FCSTD DOCUMENT  (FreeCAD 0.19R24291 (Git))
Label: Problem02
License: All rights reserved
LicenseURL: http://en.wikipedia.org/wiki/All_rights_reserved
objects: App::FeaturePython×44, Part::Part2DObjectPython×14, Part::Mirroring×13, Part::FeaturePython×1
note: 27 computed .brp shape members not serialized (recipe doc carries the construction recipe); baked Part::Feature solids carry a one-line shape summary decoded from their .brp

FEATURE [Part::Part2DObjectPython] Circle  # Draft 2D object (typed FeaturePython)
  Area = 0
  FirstAngle = 0
  LastAngle = 0
  MakeFace = false
  Radius = 40
FEATURE [Part::Part2DObjectPython] Circle001  # Draft 2D object (typed FeaturePython)
  Area = 0
  FirstAngle = 0
  LastAngle = 0
  MakeFace = false
  Radius = 60
FEATURE [Part::Part2DObjectPython] Line  # Draft 2D object (typed FeaturePython)
  Area = 0
  ChamferSize = 0
  Closed = false
  End = (7.3e-15,-60,0)
  FilletRadius = 0
  Length = 120
  MakeFace = false
  Placement = pos=(0,60,0) rot=(0,0,1;0rad)
  Points = (2) [(0,0,0),(3.67394e-15,-120,0)]
  Start = (0,60,0)
  Subdivisions = 0
FEATURE [Part::Part2DObjectPython] Line001  # Draft 2D object (typed FeaturePython)
  Area = 0
  ChamferSize = 0
  Closed = false
  End = (60,3.7e-15,0)
  FilletRadius = 0
  Length = 120
  MakeFace = false
  Placement = pos=(-60,-1.1e-14,0) rot=(0,0,1;0rad)
  Points = (2) [(0,0,0),(120,1.10218e-14,0)]
  Start = (-60,-1.1e-14,0)
  Subdivisions = 0
FEATURE [Part::FeaturePython] Array  # Draft array (typed FeaturePython)
  Angle = 360
  ArrayType = 1
  Axis = (0,0,1)
  Center = (0,0,0)
  Count = 12
  ExpandArray = false
  Fuse = false
  IntervalAxis = (0,0,0)
  IntervalX = (50,0,0)
  IntervalY = (0,50,0)
  IntervalZ = (0,0,50)
  NumberCircles = 3
  NumberPolar = 12
  NumberX = 2
  NumberY = 2
  NumberZ = 1
  PlacementList = 12 placements: [(-60,-1.10218e-14,0),(-51.9615,-30,0),(-30,-51.9615,0),(1.42109e-14,-60,0),(30,-51.9615,0),(51.9615,-30,0),(60,3.67394e-15,0),(51.9615,30,0),(30,51.9615,0),(0,60,0),(-30,51.9615,0),(-51.9615,30,0)]
  RadialDistance = 50
  ScaleList = (12) [(1,1,1),(1,1,1),(1,1,1),(1,1,1),(1,1,1),(1,1,1),(1,1,1),(1,1,1),(1,1,1),(1,1,1),(1,1,1),(1,1,1)]
  Symmetry = 1
  TangentialDistance = 25
FEATURE [Part::Part2DObjectPython] Line004  # Draft 2D object (typed FeaturePython)
  Area = 0
  ChamferSize = 0
  Closed = false
  End = (-34.641,20,0)
  FilletRadius = 0
  Length = 18.3473
  MakeFace = false
  Placement = pos=(-34.641,20,0) rot=(0,0,1;0rad)
  Points = (2) [(-18.3473,3.55271e-15,0),(0,0,0)]
  Start = (-52.9883,20,0)
  Subdivisions = 0
FEATURE [Part::Part2DObjectPython] Line005  # Draft 2D object (typed FeaturePython)
  Area = 0
  ChamferSize = 0
  Closed = false
  End = (-20,34.641,0)
  FilletRadius = 0
  Length = 11.1816
  MakeFace = false
  Placement = pos=(-20,34.641,0) rot=(0,0,1;0rad)
  Points = (2) [(-11.1816,0,0),(0,0,0)]
  Start = (-31.1816,34.641,0)
  Subdivisions = 0
FEATURE [Part::Part2DObjectPython] Line006  # Draft 2D object (typed FeaturePython)
  Area = 0
  ChamferSize = 0
  Closed = false
  End = (-30,51.7655,0)
  FilletRadius = 0
  Length = 18.1383
  MakeFace = false
  Placement = pos=(-30,12.8473,0) rot=(0,0,1;3.14159rad)
  Points = (2) [(3.55271e-15,-20.7799,0),(3.55271e-15,-38.9182,0)]
  Start = (-30,33.6272,0)
  Subdivisions = 0
FEATURE [Part::Part2DObjectPython] Line007  # Draft 2D object (typed FeaturePython)
  Area = 0
  ChamferSize = 0
  Closed = false
  End = (-51.9615,30,0)
  FilletRadius = 0
  Length = 11.2503
  MakeFace = false
  Placement = pos=(-51.9615,30,0) rot=(0,0,1;0rad)
  Points = (2) [(-7.10543e-15,-11.2503,0),(0,-3.55271e-15,0)]
  Start = (-51.9615,18.7497,0)
  Subdivisions = 0
FEATURE [Part::Mirroring] mirror  label="Line004 (mirrored)"
  Base = (0,60,0)
  Normal = (-1,1e-16,0)
  Source = -> Line004
FEATURE [Part::Mirroring] mirror001  label="Line007 (mirrored)"
  Base = (0,60,0)
  Normal = (-1,1e-16,0)
  Source = -> Line007
FEATURE [Part::Mirroring] mirror002  label="Line005 (mirrored)"
  Base = (0,60,0)
  Normal = (-1,1e-16,0)
  Source = -> Line005
FEATURE [Part::Mirroring] mirror003  label="Line006 (mirrored)"
  Base = (0,60,0)
  Normal = (-1,1e-16,0)
  Source = -> Line006
FEATURE [Part::Mirroring] mirror004  label="Line002 (mirrored)"
  Base = (-60,3.7e-15,0)
  Normal = (0,-1,0)
FEATURE [Part::Mirroring] mirror005  label="Line004 (mirrored)001"
  Base = (-60,3.7e-15,0)
  Normal = (0,-1,0)
  Source = -> Line004
FEATURE [Part::Mirroring] mirror006  label="Line007 (mirrored)001"
  Base = (-60,3.7e-15,0)
  Normal = (0,-1,0)
  Source = -> Line007
FEATURE [Part::Mirroring] mirror007  label="Line005 (mirrored)001"
  Base = (-60,3.7e-15,0)
  Normal = (0,-1,0)
  Source = -> Line005
FEATURE [Part::Mirroring] mirror008  label="Line006 (mirrored)001"
  Base = (-60,3.7e-15,0)
  Normal = (0,-1,0)
  Source = -> Line006
FEATURE [Part::Mirroring] mirror009  label="Line004 (mirrored)001 (mirrored)"
  Base = (-1.1e-14,-60,0)
  Normal = (1,-1e-16,0)
  Source = -> mirror005
FEATURE [Part::Mirroring] mirror010  label="Line007 (mirrored)001 (mirrored)"
  Base = (-1.1e-14,-60,0)
  Normal = (1,-1e-16,0)
  Source = -> mirror006
FEATURE [Part::Mirroring] mirror011  label="Line005 (mirrored)001 (mirrored)"
  Base = (-1.1e-14,-60,0)
  Normal = (1,-1e-16,0)
  Source = -> mirror007
FEATURE [Part::Mirroring] mirror012  label="Line006 (mirrored)001 (mirrored)"
  Base = (-1.1e-14,-60,0)
  Normal = (1,-1e-16,0)
  Source = -> mirror008
FEATURE [Part::Part2DObjectPython] BSpline  # Draft 2D object (typed FeaturePython)
  Area = 0
  Closed = true
  MakeFace = false
  Parameterization = 1
  Points = (12) [(-60,1.83697e-14,0),(-51.9615,20,0),(-30,34.641,0),(-6.43249e-15,40,0),(30,34.641,0),(51.9615,20,0),(60,3.67394e-15,0),(51.9615,-20,0),(30,-34.641,0),+3 more]
FEATURE [App::FeaturePython] Dimension  # Draft dimension (typed FeaturePython)
  Diameter = false
  Dimline = (45.3041,74.677,0)
  Direction = (0,0,0)
  Distance = 120
  End = (60,3.7e-15,0)
  Normal = (0,0,1)
  Start = (-60,-1.1e-14,0)
FEATURE [App::FeaturePython] Dimension001  # Draft dimension (typed FeaturePython)
  Diameter = false
  Dimline = (80.4023,-18.6692,0)
  Direction = (0,0,0)
  Distance = 80
  End = (-7.3e-15,-40,0)
  Normal = (0,0,1)
  Start = (-6.4e-15,40,0)
FEATURE [App::FeaturePython] Text  # WARN: FeaturePython — macro-defined, semantics opaque (R4)
  Placement = pos=(-55.7588,31.1154,0) rot=(0,0,1;0rad)
  Text = 1
FEATURE [App::FeaturePython] Text001  # WARN: FeaturePython — macro-defined, semantics opaque (R4)
  Placement = pos=(-33.8536,54.5142,0) rot=(0,0,1;0rad)
  Text = 2
FEATURE [App::FeaturePython] Text002  # WARN: FeaturePython — macro-defined, semantics opaque (R4)
  Placement = pos=(-1.49352,63.7244,0) rot=(0,0,1;0rad)
  Text = 3
FEATURE [App::FeaturePython] Text003  # WARN: FeaturePython — macro-defined, semantics opaque (R4)
  Placement = pos=(32.1111,54.0164,0) rot=(0,0,1;0rad)
  Text = 4
FEATURE [App::FeaturePython] Text004  # WARN: FeaturePython — macro-defined, semantics opaque (R4)
  Placement = pos=(55.261,30.8665,0) rot=(0,0,1;0rad)
  Text = 5
FEATURE [App::FeaturePython] Text005  # WARN: FeaturePython — macro-defined, semantics opaque (R4)
  Placement = pos=(61.4023,1.71218,0) rot=(0,0,1;0rad)
  Text = 6
FEATURE [App::FeaturePython] Text006  # WARN: FeaturePython — macro-defined, semantics opaque (R4)
  Placement = pos=(54.0164,-34.1025,0) rot=(0,0,1;0rad)
  Text = 7
FEATURE [App::FeaturePython] Text007  # WARN: FeaturePython — macro-defined, semantics opaque (R4)
  Placement = pos=(29.1241,-57.0034,0) rot=(0,0,1;0rad)
  Text = 8
FEATURE [App::FeaturePython] Text008  # WARN: FeaturePython — macro-defined, semantics opaque (R4)
  Placement = pos=(-1.74242,-66.4625,0) rot=(0,0,1;0rad)
  Text = 9
FEATURE [App::FeaturePython] Text009  # WARN: FeaturePython — macro-defined, semantics opaque (R4)
  Placement = pos=(-33.3557,-57.7502,0) rot=(0,0,1;0rad)
  Text = 10
FEATURE [App::FeaturePython] Text010  # WARN: FeaturePython — macro-defined, semantics opaque (R4)
  Placement = pos=(-56.2566,-34.1025,0) rot=(0,0,1;0rad)
  Text = 11
FEATURE [App::FeaturePython] Text011  # WARN: FeaturePython — macro-defined, semantics opaque (R4)
  Placement = pos=(-67.2093,-5.47628,0) rot=(0,0,1;0rad)
  Text = 12
FEATURE [App::FeaturePython] Text012  # WARN: FeaturePython — macro-defined, semantics opaque (R4)
  Placement = pos=(-63.4754,1.24465,0) rot=(0,0,1;0rad)
  Text = A
FEATURE [App::FeaturePython] Text013  # WARN: FeaturePython — macro-defined, semantics opaque (R4)
  Placement = pos=(1.24462,2.73819,0) rot=(0,0,1;0rad)
  Text = O
FEATURE [App::FeaturePython] Text014  # WARN: FeaturePython — macro-defined, semantics opaque (R4)
  Placement = pos=(61.4023,-4.36853,0) rot=(0,0,1;0rad)
  Text = B
FEATURE [App::FeaturePython] Text015  # WARN: FeaturePython — macro-defined, semantics opaque (R4)
  Placement = pos=(-59.2509,-4.7914,0) rot=(0,0,1;0rad)
  Text = P12
FEATURE [App::FeaturePython] Text016  # WARN: FeaturePython — macro-defined, semantics opaque (R4)
  Placement = pos=(-51.6501,14.3628,0) rot=(0,0,1;0rad)
  Text = P1
FEATURE [App::FeaturePython] Text017  # WARN: FeaturePython — macro-defined, semantics opaque (R4)
  Placement = pos=(-33.4079,29.5646,0) rot=(0,0,1;0rad)
  Text = P2
FEATURE [App::FeaturePython] Text018  # WARN: FeaturePython — macro-defined, semantics opaque (R4)
  Placement = pos=(-6.6528,35.6453,0) rot=(0,0,1;0rad)
  Text = P3
FEATURE [App::FeaturePython] Text019  # WARN: FeaturePython — macro-defined, semantics opaque (R4)
  Placement = pos=(28.0073,28.6525,0) rot=(0,0,1;0rad)
  Text = P4
FEATURE [App::FeaturePython] Text020  # WARN: FeaturePython — macro-defined, semantics opaque (R4)
  Placement = pos=(48.0737,13.4507,0) rot=(0,0,1;0rad)
  Text = P5
FEATURE [App::FeaturePython] Text021  # WARN: FeaturePython — macro-defined, semantics opaque (R4)
  Placement = pos=(53.2423,-5.09545,0) rot=(0,0,1;0rad)
  Text = P6
FEATURE [App::FeaturePython] Text022  # WARN: FeaturePython — macro-defined, semantics opaque (R4)
  Placement = pos=(46.8575,-17.8649,0) rot=(0,0,1;0rad)
  Text = P7
FEATURE [App::FeaturePython] Text023  # WARN: FeaturePython — macro-defined, semantics opaque (R4)
  Placement = pos=(27.3992,-33.0667,0) rot=(0,0,1;0rad)
  Text = P8
FEATURE [App::FeaturePython] Text024  # WARN: FeaturePython — macro-defined, semantics opaque (R4)
  Placement = pos=(-6.04468,-37.6273,0) rot=(0,0,1;0rad)
  Text = P9
FEATURE [App::FeaturePython] Text025  # WARN: FeaturePython — macro-defined, semantics opaque (R4)
  Placement = pos=(-33.4079,-32.7627,0) rot=(0,0,1;0rad)
  Text = P10
FEATURE [App::FeaturePython] Text026  # WARN: FeaturePython — macro-defined, semantics opaque (R4)
  Placement = pos=(-51.65,-17.8649,0) rot=(0,0,1;0rad)
  Text = P11
FEATURE [App::FeaturePython] Text027  # WARN: FeaturePython — macro-defined, semantics opaque (R4)
  Placement = pos=(-31.8877,18.9234,0) rot=(0,0,1;0rad)
  Text = 1'
FEATURE [App::FeaturePython] Text028  # WARN: FeaturePython — macro-defined, semantics opaque (R4)
  Placement = pos=(-18.2061,31.0848,0) rot=(0,0,1;0rad)
  Text = 2'
FEATURE [App::FeaturePython] Text029  # WARN: FeaturePython — macro-defined, semantics opaque (R4)
  Placement = pos=(1.55618,34.1252,0) rot=(0,0,1;0rad)
  Text = 3'
FEATURE [App::FeaturePython] Text030  # WARN: FeaturePython — macro-defined, semantics opaque (R4)
  Placement = pos=(19.4943,26.8283,0) rot=(0,0,1;0rad)
  Text = 4'
FEATURE [App::FeaturePython] Text031  # WARN: FeaturePython — macro-defined, semantics opaque (R4)
  Placement = pos=(31.3517,14.6669,0) rot=(0,0,1;0rad)
  Text = 5'
FEATURE [App::FeaturePython] Text032  # WARN: FeaturePython — macro-defined, semantics opaque (R4)
  Placement = pos=(35.6082,0.985281,0) rot=(0,0,1;0rad)
  Text = 6'
FEATURE [App::FeaturePython] Text033  # WARN: FeaturePython — macro-defined, semantics opaque (R4)
  Placement = pos=(32.5678,-17.5609,0) rot=(0,0,1;0rad)
  Text = 7'
FEATURE [App::FeaturePython] Text034  # WARN: FeaturePython — macro-defined, semantics opaque (R4)
  Placement = pos=(19.7983,-31.2425,0) rot=(0,0,1;0rad)
  Text = 8'
FEATURE [App::FeaturePython] Text035  # WARN: FeaturePython — macro-defined, semantics opaque (R4)
  Placement = pos=(0.948107,-38.8434,0) rot=(0,0,1;0rad)
  Text = 9'
FEATURE [App::FeaturePython] Text036  # WARN: FeaturePython — macro-defined, semantics opaque (R4)
  Placement = pos=(-17.5981,-34.5869,0) rot=(0,0,1;0rad)
  Text = 10'
FEATURE [App::FeaturePython] Text037  # WARN: FeaturePython — macro-defined, semantics opaque (R4)
  Placement = pos=(-35.2321,-17.5609,0) rot=(0,0,1;0rad)
  Text = 11'
FEATURE [App::FeaturePython] Text038  # WARN: FeaturePython — macro-defined, semantics opaque (R4)
  Placement = pos=(-38.5765,0.681248,0) rot=(0,0,1;0rad)
  Text = 12'
FEATURE [App::FeaturePython] Text039  # WARN: FeaturePython — macro-defined, semantics opaque (R4)
  Placement = pos=(-3.61243,41.726,0) rot=(0,0,1;0rad)
  Text = C
FEATURE [App::FeaturePython] Text040  # WARN: FeaturePython — macro-defined, semantics opaque (R4)
  Placement = pos=(-3.61243,-45.2281,0) rot=(0,0,1;0rad)
  Text = D
FEATURE [App::FeaturePython] Text041  # WARN: FeaturePython — macro-defined, semantics opaque (R4)
  Placement = pos=(-27.9353,-76.8478,0) rot=(0,0,1;0rad)
  Text = All Dimensions are in 'mm'
FEATURE [Part::Part2DObjectPython] Line008  # Draft 2D object (typed FeaturePython)
  Area = 0
  ChamferSize = 0
  Closed = false
  End = (7.3e-15,-60,0)
  FilletRadius = 0
  Length = 120
  MakeFace = false
  Placement = pos=(0,60,0) rot=(0,0,1;0rad)
  Points = (2) [(0,0,0),(3.67394e-15,-120,0)]
  Start = (0,60,0)
  Subdivisions = 0
FEATURE [Part::Part2DObjectPython] Line009  # Draft 2D object (typed FeaturePython)
  Area = 0
  ChamferSize = 0
  Closed = false
  End = (30,-51.9615,0)
  FilletRadius = 0
  Length = 119.83
  MakeFace = false
  Placement = pos=(-30,51.7655,0) rot=(0,0,1;0rad)
  Points = (2) [(0,0,0),(60,-103.727,0)]
  Start = (-30,51.7655,0)
  Subdivisions = 0
FEATURE [Part::Part2DObjectPython] Line010  # Draft 2D object (typed FeaturePython)
  Area = 0
  ChamferSize = 0
  Closed = false
  End = (51.9615,-30,0)
  FilletRadius = 0
  Length = 120
  MakeFace = false
  Placement = pos=(-51.9615,30,0) rot=(0,0,1;0rad)
  Points = (2) [(0,0,0),(103.923,-60,0)]
  Start = (-51.9615,30,0)
  Subdivisions = 0
FEATURE [Part::Part2DObjectPython] Line011  # Draft 2D object (typed FeaturePython)
  Area = 0
  ChamferSize = 0
  Closed = false
  End = (-30,-51.7655,0)
  FilletRadius = 0
  Length = 119.661
  MakeFace = false
  Placement = pos=(30,51.7655,0) rot=(0,0,1;0rad)
  Points = (2) [(0,0,0),(-60,-103.531,0)]
  Start = (30,51.7655,0)
  Subdivisions = 0
FEATURE [Part::Part2DObjectPython] Line012  # Draft 2D object (typed FeaturePython)
  Area = 0
  ChamferSize = 0
  Closed = false
  End = (-51.9615,-30,0)
  FilletRadius = 0
  Length = 120
  MakeFace = false
  Placement = pos=(51.9615,30,0) rot=(0,0,1;0rad)
  Points = (2) [(0,0,0),(-103.923,-60,0)]
  Start = (51.9615,30,0)
  Subdivisions = 0
